# Revit family: QMXE
name_source: partatom
category: Mechanical Equipment
units: mm (PartAtom-declared; Revit-internal decimal feet)

## family parameters
Always vertical = Yes
Cut with Voids When Loaded = No
Part Type = Normal
Room Calculation Point = No
Round Connector Dimension = Use Diameter
Shared = No
Work Plane-Based = No

## types (22) — shared parameters
0 = 0' - 0"
1" = 0' - 1"
1.5 = 0' - 1 1/2"
2" = 0' - 2"
2' = 2' - 0"
3" = 0' - 3"
4" = 0' - 4"
C = 0' - 3"
C/2 = 0' - 1 1/2"
Manufacturer = Loren Cook Company
ONE EIGTH = 0' - 0 1/8"
URL = www.lorencook.com

## per-type parameters (varying)
| type | (B/2)-.125" | (FAN_RADIUS)*.75 | A | A/2 | B | B/2 | D | D-(G/2) | DC/2 | DUCT_COLLAR | E | F | FAN_DIA | FAN_RAD+1.5" | FAN_RADIUS | FAN_RADIUS/5 | G | G/2 | MC_LENGTH | Model | QMX_LENGTH | T_SQ | T_SQ/2 | Type Comments |
| 90_QMXE | 0' - 9 7/8" | 0' - 4 13/16" | 3' - 3 3/16" | 1' - 7 19/32" | 1' - 8" | 0' - 10" | 3' - 1 3/8" | 1' - 11 3/32" | 0' - 6 13/32" | 1' - 0 13/16" | 1' - 10 1/2" | 1' - 9 1/4" | 1' - 0 13/16" | 0' - 7 29/32" | 0' - 6 13/32" | 0' - 1 9/32" | 2' - 4 9/16" | 1' - 2 9/32" | -1' - 3 29/32" | QMXE | 1' - 7 7/8" | 1' - 3 1/2" | 0' - 7 3/4" | Mixed-Flow Exhaust Blower Low Pressure Belt Drive Arrangement 9 |
| 300_QMXE | 2' - 2 7/8" | 1' - 3 15/16" | 6' - 2 1/2" | 3' - 1 1/4" | 4' - 6" | 2' - 3" | 6' - 10" | 3' - 9 3/16" | 1' - 9 1/4" | 3' - 6 1/2" | 3' - 4" | 3' - 1 5/8" | 3' - 6 1/2" | 1' - 10 3/4" | 1' - 9 1/4" | 0' - 4 1/4" | 6' - 1 5/8" | 3' - 0 13/16" | -3' - 7 3/16" | QMXE | 4' - 6" | 4' - 1 1/2" | 2' - 0 3/4" | Mixed-Flow Exhaust Blower Low Pressure Belt Drive Arrangement 9 |
| 120_QMXE | 0' - 11 7/8" | 0' - 6 13/32" | 3' - 3 5/8" | 1' - 7 13/16" | 2' - 0" | 1' - 0" | 3' - 7 5/8" | 2' - 3 7/32" | 0' - 8 17/32" | 1' - 5 1/16" | 2' - 1 3/8" | 2' - 0 3/8" | 1' - 5 1/16" | 0' - 10 1/32" | 0' - 8 17/32" | 0' - 1 23/32" | 2' - 8 13/16" | 1' - 4 13/32" | -1' - 7 3/16" | QMXE | 2' - 0" | 1' - 7 1/2" | 0' - 9 3/4" | Mixed-Flow Exhaust Blower Low Pressure Belt Drive Arrangement 9 |
| 135_QMXE | 1' - 0 7/8" | 0' - 7 7/32" | 3' - 7 15/16" | 1' - 9 31/32" | 2' - 2" | 1' - 1" | 3' - 10 1/2" | 2' - 0 23/32" | 0' - 9 5/8" | 1' - 7 1/4" | 2' - 3 1/4" | 2' - 1 3/8" | 1' - 7 1/4" | 0' - 11 1/8" | 0' - 9 5/8" | 0' - 1 15/16" | 3' - 7 9/16" | 1' - 9 25/32" | -1' - 9 19/32" | QMXE | 2' - 3" | 1' - 9 1/2" | 0' - 10 3/4" | Mixed-Flow Exhaust Blower Low Pressure Belt Drive Arrangement 9 |
| 150_QMXE | 1' - 2 7/8" | 0' - 8 1/32" | 3' - 10 15/16" | 1' - 11 15/32" | 2' - 6" | 1' - 3" | 4' - 3" | 2' - 5 7/32" | 0' - 10 11/16" | 1' - 9 3/8" | 2' - 4" | 2' - 2 1/8" | 1' - 9 3/8" | 1' - 0 3/16" | 0' - 10 11/16" | 0' - 2 1/8" | 3' - 7 9/16" | 1' - 9 25/32" | -2' - 0" | QMXE | 2' - 6" | 2' - 1 1/2" | 1' - 0 3/4" | Mixed-Flow Exhaust Blower Low Pressure Belt Drive Arrangement 9 |
| 165_QMXE | 1' - 5 3/8" | 0' - 8 13/16" | 4' - 3 1/8" | 2' - 1 9/16" | 2' - 11" | 1' - 5 1/2" | 4' - 7" | 2' - 7 3/16" | 0' - 11 3/4" | 1' - 11 1/2" | 2' - 5 13/16" | 2' - 3 1/8" | 1' - 11 1/2" | 1' - 1 1/4" | 0' - 11 3/4" | 0' - 2 11/32" | 3' - 11 5/8" | 1' - 11 13/16" | -2' - 2 13/32" | QMXE | 2' - 9" | 2' - 6 1/2" | 1' - 3 1/4" | Mixed-Flow Exhaust Blower Low Pressure Belt Drive Arrangement 9 |
| 180_QMXE | 1' - 6 3/8" | 0' - 9 5/8" | 4' - 9 3/4" | 2' - 4 7/8" | 3' - 1" | 1' - 6 1/2" | 4' - 9 3/4" | 2' - 7 7/16" | 1' - 0 13/16" | 2' - 1 5/8" | 2' - 6 3/4" | 2' - 4 1/8" | 2' - 1 5/8" | 1' - 2 5/16" | 1' - 0 13/16" | 0' - 2 9/16" | 4' - 4 5/8" | 2' - 2 5/16" | -2' - 4" | QMXE | 2' - 11" | 2' - 8 1/2" | 1' - 4 1/4" | Mixed-Flow Exhaust Blower Low Pressure Belt Drive Arrangement 9 |
| 202_QMXE | 1' - 7 7/8" | 0' - 9 5/8" | 5' - 0 1/2" | 2' - 6 1/4" | 3' - 4" | 1' - 8" | 5' - 1 13/16" | 2' - 6 1/2" | 1' - 2 3/8" | 2' - 4 3/4" | 2' - 8 1/8" | 2' - 5 1/2" | 2' - 1 5/8" | 1' - 2 5/16" | 1' - 0 13/16" | 0' - 2 9/16" | 5' - 2 5/8" | 2' - 7 5/16" | -2' - 4" | QMXE | 2' - 11" | 2' - 11 1/2" | 1' - 5 3/4" | Mixed-Flow Exhaust Blower Low Pressure Belt Drive Arrangement 9 |
| 225_QMXE | 1' - 9 3/8" | 0' - 11 31/32" | 5' - 4" | 2' - 8" | 3' - 7" | 1' - 9 1/2" | 5' - 8 1/8" | 3' - 0 13/16" | 1' - 3 31/32" | 2' - 7 15/16" | 2' - 11 1/2" | 2' - 9" | 2' - 7 15/16" | 1' - 5 15/32" | 1' - 3 31/32" | 0' - 3 3/16" | 5' - 2 5/8" | 2' - 7 5/16" | -2' - 8 13/16" | QMXE | 3' - 5" | 3' - 2 1/2" | 1' - 7 1/4" | Mixed-Flow Exhaust Blower Low Pressure Belt Drive Arrangement 9 |
| 245_QMXE | 1' - 10 7/8" | 1' - 1 1/32" | 5' - 4 7/16" | 2' - 8 7/32" | 3' - 10" | 1' - 11" | 5' - 11 13/16" | 2' - 11" | 1' - 5 3/8" | 2' - 10 3/4" | 3' - 0 5/8" | 2' - 10 1/8" | 2' - 10 3/4" | 1' - 6 7/8" | 1' - 5 3/8" | 0' - 3 15/32" | 6' - 1 5/8" | 3' - 0 13/16" | -2' - 11 19/32" | QMXE | 3' - 8 1/2" | 3' - 5 1/2" | 1' - 8 3/4" | Mixed-Flow Exhaust Blower Low Pressure Belt Drive Arrangement 9 |
| 270_QMXE | 2' - 0 7/8" | 1' - 2 3/8" | 5' - 7 3/16" | 2' - 9 19/32" | 4' - 2" | 2' - 1" | 6' - 4 5/16" | 3' - 3 1/2" | 1' - 7 5/32" | 3' - 2 5/16" | 3' - 2" | 2' - 11 9/16" | 3' - 2 5/16" | 1' - 8 21/32" | 1' - 7 5/32" | 0' - 3 27/32" | 6' - 1 5/8" | 3' - 0 13/16" | -3' - 1 19/32" | QMXE | 3' - 11" | 3' - 9 1/2" | 1' - 10 3/4" | Mixed-Flow Exhaust Blower Low Pressure Belt Drive Arrangement 9 |
| 120_QMXE-HP | 0' - 11 7/8" | 0' - 6 13/32" | 3' - 3 5/8" | 1' - 7 13/16" | 2' - 0" | 1' - 0" | 3' - 7 5/8" | 2' - 3 7/32" | 0' - 8 17/32" | 1' - 5 1/16" | 2' - 1 3/8" | 2' - 0 3/8" | 1' - 5 1/16" | 0' - 10 1/32" | 0' - 8 17/32" | 0' - 1 23/32" | 2' - 8 13/16" | 1' - 4 13/32" | -1' - 7 3/16" | QMXE-HP | 2' - 0" | 1' - 7 1/2" | 0' - 9 3/4" | Mixed-Flow Exhaust Blower High Pressure Belt Drive Arrangement 9 |
| 135_QMXE-HP | 1' - 0 7/8" | 0' - 7 7/32" | 3' - 7 15/16" | 1' - 9 31/32" | 2' - 2" | 1' - 1" | 3' - 10 1/2" | 2' - 0 23/32" | 0' - 9 5/8" | 1' - 7 1/4" | 2' - 3 1/4" | 2' - 1 3/8" | 1' - 7 1/4" | 0' - 11 1/8" | 0' - 9 5/8" | 0' - 1 15/16" | 3' - 7 9/16" | 1' - 9 25/32" | -1' - 9 19/32" | QMXE-HP | 2' - 3" | 1' - 9 1/2" | 0' - 10 3/4" | Mixed-Flow Exhaust Blower High Pressure Belt Drive Arrangement 9 |
| 150_QMXE-HP | 1' - 2 7/8" | 0' - 8 1/32" | 3' - 10 15/16" | 1' - 11 15/32" | 2' - 6" | 1' - 3" | 4' - 3" | 2' - 5 7/32" | 0' - 10 11/16" | 1' - 9 3/8" | 2' - 4" | 2' - 2 1/8" | 1' - 9 3/8" | 1' - 0 3/16" | 0' - 10 11/16" | 0' - 2 1/8" | 3' - 7 9/16" | 1' - 9 25/32" | -2' - 0" | QMXE-HP | 2' - 6" | 2' - 1 1/2" | 1' - 0 3/4" | Mixed-Flow Exhaust Blower High Pressure Belt Drive Arrangement 9 |
| 165_QMXE-HP | 1' - 5 3/8" | 0' - 8 13/16" | 4' - 3 1/8" | 2' - 1 9/16" | 2' - 11" | 1' - 5 1/2" | 4' - 7" | 2' - 7 3/16" | 0' - 11 3/4" | 1' - 11 1/2" | 2' - 5 13/16" | 2' - 3 1/8" | 1' - 11 1/2" | 1' - 1 1/4" | 0' - 11 3/4" | 0' - 2 11/32" | 3' - 11 5/8" | 1' - 11 13/16" | -2' - 2 13/32" | QMXE-HP | 2' - 9" | 2' - 6 1/2" | 1' - 3 1/4" | Mixed-Flow Exhaust Blower High Pressure Belt Drive Arrangement 9 |
| 180_QMXE-HP | 1' - 6 3/8" | 0' - 9 5/8" | 4' - 9 3/4" | 2' - 4 7/8" | 3' - 1" | 1' - 6 1/2" | 4' - 9 3/4" | 2' - 7 7/16" | 1' - 0 13/16" | 2' - 1 5/8" | 2' - 6 3/4" | 2' - 4 1/8" | 2' - 1 5/8" | 1' - 2 5/16" | 1' - 0 13/16" | 0' - 2 9/16" | 4' - 4 5/8" | 2' - 2 5/16" | -2' - 4" | QMXE-HP | 2' - 11" | 2' - 8 1/2" | 1' - 4 1/4" | Mixed-Flow Exhaust Blower High Pressure Belt Drive Arrangement 9 |
| 202_QMXE-HP | 1' - 7 7/8" | 0' - 9 5/8" | 5' - 0 1/2" | 2' - 6 1/4" | 3' - 4" | 1' - 8" | 5' - 1 13/16" | 2' - 6 1/2" | 1' - 2 3/8" | 2' - 4 3/4" | 2' - 8 1/8" | 2' - 5 1/2" | 2' - 1 5/8" | 1' - 2 5/16" | 1' - 0 13/16" | 0' - 2 9/16" | 5' - 2 5/8" | 2' - 7 5/16" | -2' - 4" | QMXE-HP | 2' - 11" | 2' - 11 1/2" | 1' - 5 3/4" | Mixed-Flow Exhaust Blower High Pressure Belt Drive Arrangement 9 |
| 225_QMXE-HP | 1' - 9 3/8" | 0' - 11 31/32" | 5' - 4" | 2' - 8" | 3' - 7" | 1' - 9 1/2" | 5' - 8 1/8" | 3' - 0 13/16" | 1' - 3 31/32" | 2' - 7 15/16" | 2' - 11 1/2" | 2' - 9" | 2' - 7 15/16" | 1' - 5 15/32" | 1' - 3 31/32" | 0' - 3 3/16" | 5' - 2 5/8" | 2' - 7 5/16" | -2' - 8 13/16" | QMXE-HP | 3' - 5" | 3' - 2 1/2" | 1' - 7 1/4" | Mixed-Flow Exhaust Blower High Pressure Belt Drive Arrangement 9 |
| 245_QMXE-HP | 1' - 10 7/8" | 1' - 1 1/32" | 5' - 4 7/16" | 2' - 8 7/32" | 3' - 10" | 1' - 11" | 5' - 11 13/16" | 2' - 11" | 1' - 5 3/8" | 2' - 10 3/4" | 3' - 0 5/8" | 2' - 10 1/8" | 2' - 10 3/4" | 1' - 6 7/8" | 1' - 5 3/8" | 0' - 3 15/32" | 6' - 1 5/8" | 3' - 0 13/16" | -2' - 11 19/32" | QMXE-HP | 3' - 8 1/2" | 3' - 5 1/2" | 1' - 8 3/4" | Mixed-Flow Exhaust Blower High Pressure Belt Drive Arrangement 9 |
| 270_QMXE-HP | 2' - 0 7/8" | 1' - 2 3/8" | 5' - 7 3/16" | 2' - 9 19/32" | 4' - 2" | 2' - 1" | 6' - 4 5/16" | 3' - 3 1/2" | 1' - 7 5/32" | 3' - 2 5/16" | 3' - 2" | 2' - 11 9/16" | 3' - 2 5/16" | 1' - 8 21/32" | 1' - 7 5/32" | 0' - 3 27/32" | 6' - 1 5/8" | 3' - 0 13/16" | -3' - 1 19/32" | QMXE-HP | 3' - 11" | 3' - 9 1/2" | 1' - 10 3/4" | Mixed-Flow Exhaust Blower High Pressure Belt Drive Arrangement 9 |
| 300_QMXE-HP | 2' - 2 7/8" | 1' - 3 15/16" | 6' - 2 1/2" | 3' - 1 1/4" | 4' - 6" | 2' - 3" | 6' - 10" | 3' - 9 3/16" | 1' - 9 1/4" | 3' - 6 1/2" | 3' - 4" | 3' - 1 5/8" | 3' - 6 1/2" | 1' - 10 3/4" | 1' - 9 1/4" | 0' - 4 1/4" | 6' - 1 5/8" | 3' - 0 13/16" | -3' - 7 3/16" | QMXE-HP | 4' - 6" | 4' - 1 1/2" | 2' - 0 3/4" | Mixed-Flow Exhaust Blower High Pressure Belt Drive Arrangement 9 |
| 90_QMXE-HP | 0' - 9 7/8" | 0' - 4 13/16" | 3' - 3 3/16" | 1' - 7 19/32" | 1' - 8" | 0' - 10" | 3' - 1 3/8" | 1' - 11 3/32" | 0' - 6 13/32" | 1' - 0 13/16" | 1' - 10 1/2" | 1' - 9 1/4" | 1' - 0 13/16" | 0' - 7 29/32" | 0' - 6 13/32" | 0' - 1 9/32" | 2' - 4 9/16" | 1' - 2 9/32" | -1' - 3 29/32" | QMXE-HP | 1' - 7 7/8" | 1' - 3 1/2" | 0' - 7 3/4" | Mixed-Flow Exhaust Blower High Pressure Belt Drive Arrangement 9 |

## geometry (parser evidence)
native form markers: Sweep x1
no freeform markers — native parametric forms only
